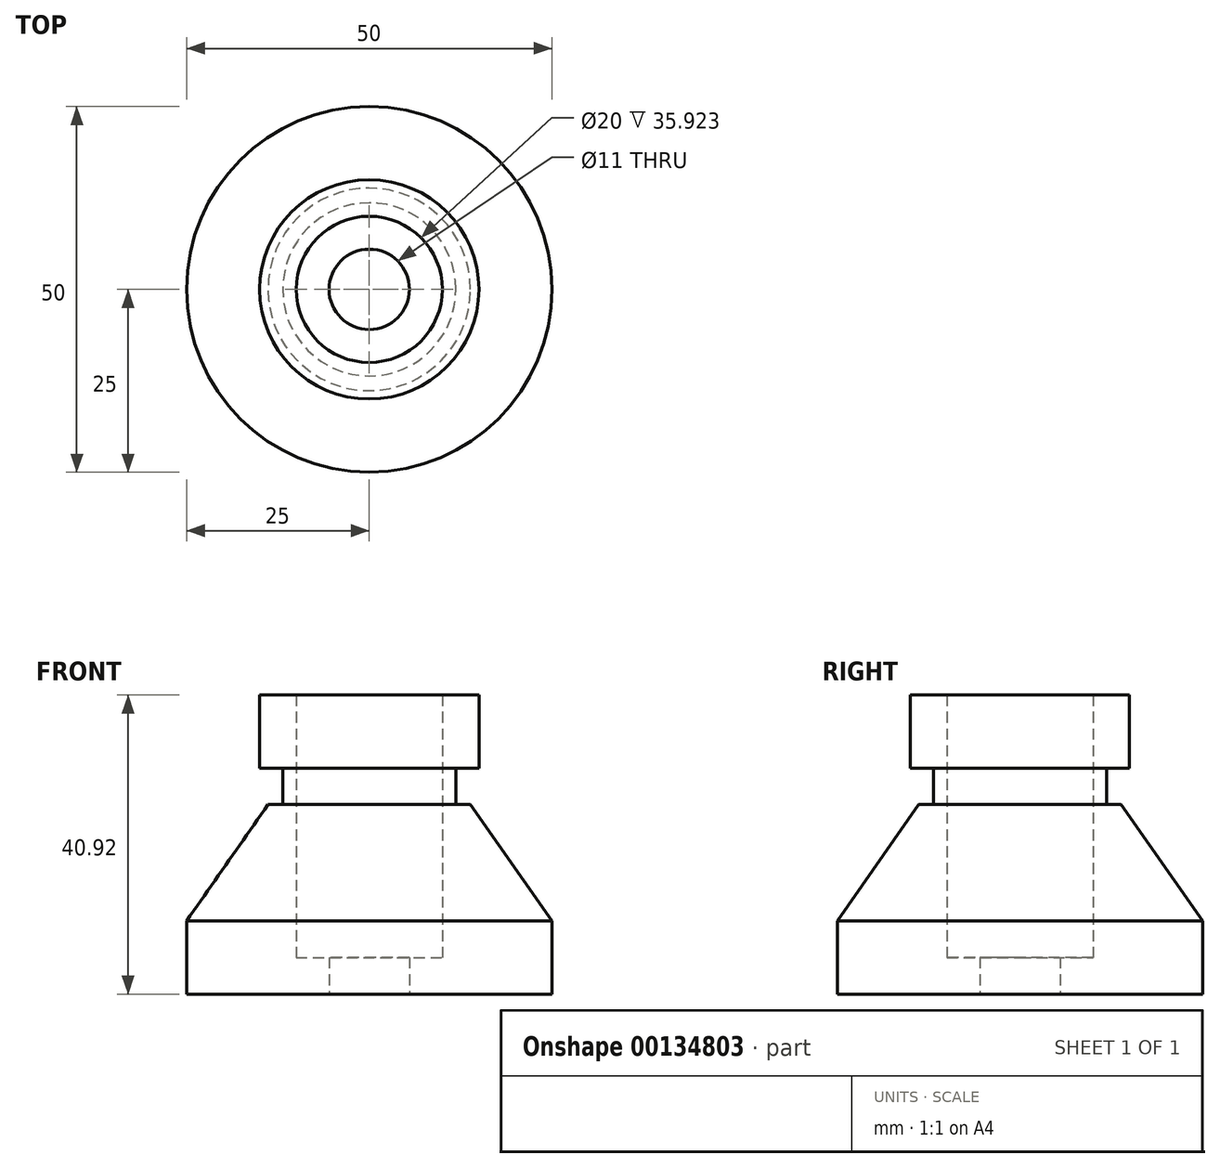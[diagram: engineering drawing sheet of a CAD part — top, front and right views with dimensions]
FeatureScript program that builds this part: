
annotation { "Feature Type Name" : "Feature", "Feature Type Description" : "" }
export const myFeature = defineFeature(function(context is Context, id is Id, definition is map)
    precondition{}
    {
        {
            var Q0;
            Q0=qCreatedBy(makeId("Front.planeOp"),FACE);
            var sketch = newSketch(context, id + "F0", { "sketchPlane" : qUnion([Q0])});
            skLineSegment(sketch, "E0", {"start": v(0, 0) * mm, "end": v(0, 50) * mm, "construction": true});
            skLineSegment(sketch, "E1", {"start": v(0, 0) * mm, "end": v(-25, 0) * mm});
            skLineSegment(sketch, "E2", {"start": v(-25, 0) * mm, "end": v(-25, 10) * mm});
            skLineSegment(sketch, "E3", {"start": v(-25, 10) * mm, "end": v(-13.85, 25.92) * mm});
            skLineSegment(sketch, "E4", {"start": v(-13.85, 25.92) * mm, "end": v(-11.85, 25.92) * mm});
            skLineSegment(sketch, "E5", {"start": v(-11.85, 25.92) * mm, "end": v(-11.85, 30.92) * mm});
            skLineSegment(sketch, "E6", {"start": v(-11.85, 30.92) * mm, "end": v(-15, 30.92) * mm});
            skLineSegment(sketch, "E7", {"start": v(-15, 30.92) * mm, "end": v(-15, 40.92) * mm});
            skLineSegment(sketch, "E8", {"start": v(-15, 40.92) * mm, "end": v(-10, 40.92) * mm});
            skLineSegment(sketch, "E9", {"start": v(-10, 40.92) * mm, "end": v(-10, 5) * mm});
            skLineSegment(sketch, "E10", {"start": v(-10, 5) * mm, "end": v(0, 5) * mm});
            skLineSegment(sketch, "E11", {"start": v(0, 5) * mm, "end": v(0, 0) * mm});
            skSolve(sketch);
        }
        {
            var Q0;
            Q0=makeQuery(id+"F0.imprint","IMPRINT",FACE,{"disambiguationData":[TD([[makeQuery(id+"F0.imprint","IMPRINT",EDGE,{"derivedFrom":sQuery(id+"F0.wireOp",EDGE,"E1")}),-1.0]])]});
            var Q1;
            Q1=sQuery(id+"F0.wireOp",EDGE,"E0");
            revolve(context, id + "F1", {"entities" : qUnion([Q0]), "axis" : qUnion([Q1]), "revolveType" : RevolveType.FULL});
        }
        {
            var Q0;
            Q0=makeQuery(id+"F1.opRevolve","SWEPT_FACE",FACE,{"disambiguationData":[OSD([sQuery(id+"F0.wireOp",EDGE,"E1")])]});
            var sketch = newSketch(context, id + "F2", { "sketchPlane" : qUnion([Q0])});
            skCircle(sketch, "E12", {"center": v(0, 0) * mm, "radius": 5.5 * mm});
            skSolve(sketch);
        }
        {
            var Q0;
            Q0=makeQuery(id+"F2.imprint","IMPRINT",FACE,{"disambiguationData":[TD([[makeQuery(id+"F2.imprint","IMPRINT",EDGE,{"derivedFrom":sQuery(id+"F2.wireOp",EDGE,"E12")}),1.0]])]});
            extrude(context, id + "F3", {"entities" : qUnion([Q0]), "operationType" : NewBodyOperationType.REMOVE, "oppositeDirection" : true, "depth" : 25 * mm});
        }
    });
